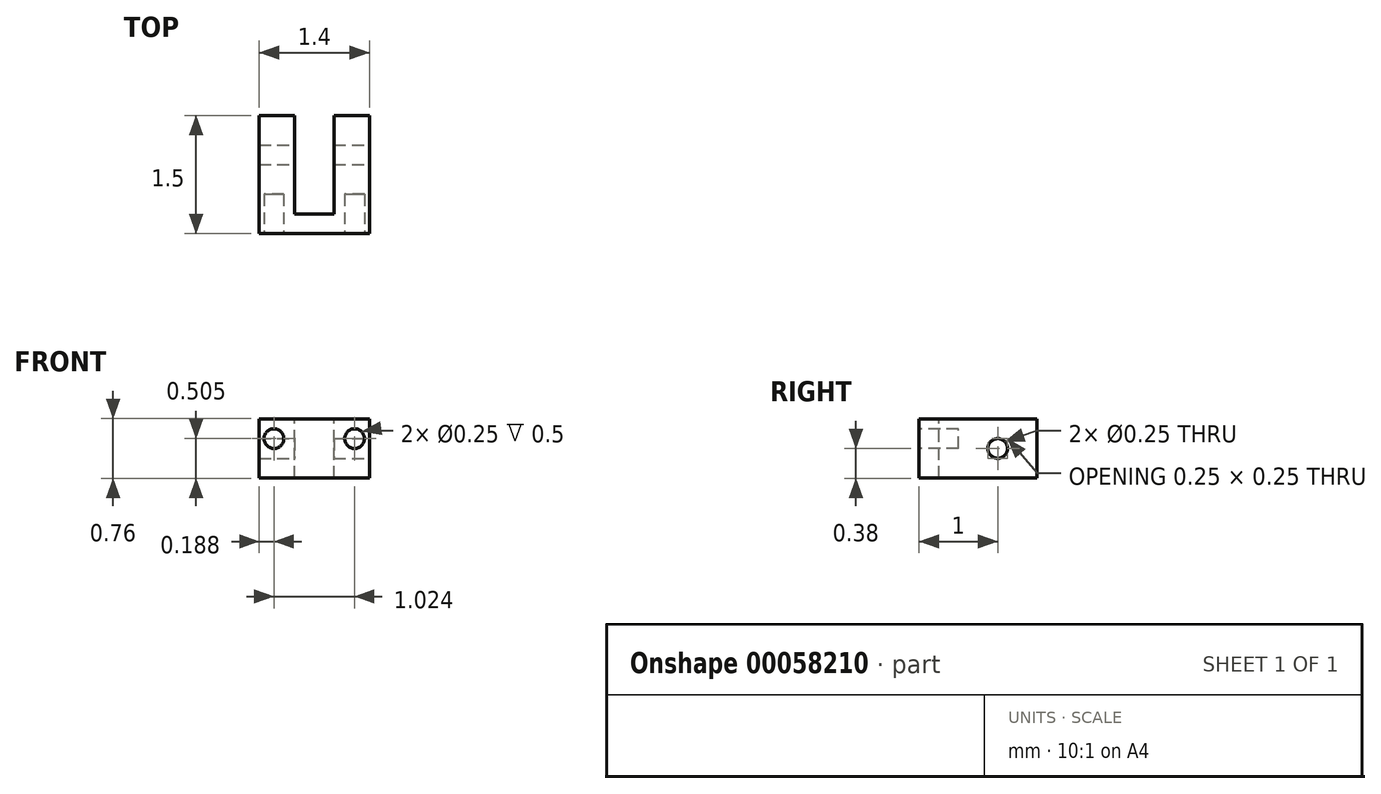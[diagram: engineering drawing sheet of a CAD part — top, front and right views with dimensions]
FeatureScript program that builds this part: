
annotation { "Feature Type Name" : "Feature", "Feature Type Description" : "" }
export const myFeature = defineFeature(function(context is Context, id is Id, definition is map)
    precondition{}
    {
        {
            var Q0;
            Q0=qCreatedBy(makeId("Front.planeOp"),FACE);
            var sketch = newSketch(context, id + "F0", { "sketchPlane" : qUnion([Q0])});
            skLineSegment(sketch, "E0.rect.bottom", {"start": v(0.7, 0.37) * mm, "end": v(-0.7, 0.37) * mm});
            skLineSegment(sketch, "E0.rect.top", {"start": v(0.7, -0.38) * mm, "end": v(-0.7, -0.38) * mm});
            skLineSegment(sketch, "E0.rect.left", {"start": v(0.7, 0.37) * mm, "end": v(0.7, -0.38) * mm});
            skLineSegment(sketch, "E0.rect.right", {"start": v(-0.7, 0.37) * mm, "end": v(-0.7, -0.38) * mm});
            skPoint(sketch, "E0.rect.middle", {"position": v(0, 0) * mm});
            skSolve(sketch);
        }
        {
            var Q0;
            Q0=qSketchRegion(id+"F0",true);
            extrude(context, id + "F1", {"entities" : qUnion([Q0]), "endBound" : BoundingType.SYMMETRIC, "depth" : 1.5 * mm});
        }
        {
            var Q0;
            Q0=makeQuery(id+"F1.opExtrude","SWEPT_FACE",FACE,{"disambiguationData":[OSD([sQuery(id+"F0.wireOp",EDGE,"E0.rect.left")])]});
            var sketch = newSketch(context, id + "F2", { "sketchPlane" : qUnion([Q0])});
            skCircle(sketch, "E1", {"center": v(0.25, 0) * mm, "radius": 0.12 * mm});
            skSolve(sketch);
        }
        {
            var Q0;
            Q0=qSketchRegion(id+"F2",true);
            extrude(context, id + "F3", {"entities" : qUnion([Q0]), "operationType" : NewBodyOperationType.REMOVE, "oppositeDirection" : true, "depth" : 25 * mm});
        }
        {
            var Q0;
            Q0=makeQuery(id+"F1.opExtrude","SWEPT_FACE",FACE,{"disambiguationData":[OSD([sQuery(id+"F0.wireOp",EDGE,"E0.rect.bottom")])]});
            var sketch = newSketch(context, id + "F4", { "sketchPlane" : qUnion([Q0])});
            skLineSegment(sketch, "E2.bottom", {"start": v(-0.25, 0.75) * mm, "end": v(0.25, 0.75) * mm});
            skLineSegment(sketch, "E2.top", {"start": v(-0.25, -0.5) * mm, "end": v(0.25, -0.5) * mm});
            skLineSegment(sketch, "E2.left", {"start": v(-0.25, 0.75) * mm, "end": v(-0.25, -0.5) * mm});
            skLineSegment(sketch, "E2.right", {"start": v(0.25, 0.75) * mm, "end": v(0.25, -0.5) * mm});
            skSolve(sketch);
        }
        {
            var Q0;
            Q0=qSketchRegion(id+"F4",true);
            extrude(context, id + "F5", {"entities" : qUnion([Q0]), "operationType" : NewBodyOperationType.REMOVE, "endBound" : BoundingType.SYMMETRIC, "oppositeDirection" : true, "depth" : 25 * mm});
        }
        {
            var Q0;
            Q0=makeQuery(id+"F1.opExtrude","CAP_FACE",FACE,{"disambiguationData":[OSD([sQuery(id+"F0.wireOp",EDGE,"E0.rect.bottom"),sQuery(id+"F0.wireOp",EDGE,"E0.rect.top"),sQuery(id+"F0.wireOp",EDGE,"E0.rect.left"),sQuery(id+"F0.wireOp",EDGE,"E0.rect.right")])],"isStart":false});
            var sketch = newSketch(context, id + "F6", { "sketchPlane" : qUnion([Q0])});
            skCircle(sketch, "E3", {"center": v(0.51, 0.12) * mm, "radius": 0.12 * mm});
            skCircle(sketch, "E4", {"center": v(-0.51, 0.12) * mm, "radius": 0.12 * mm});
            skSolve(sketch);
        }
        {
            var Q0;
            Q0=qSketchRegion(id+"F6",true);
            extrude(context, id + "F7", {"entities" : qUnion([Q0]), "operationType" : NewBodyOperationType.REMOVE, "oppositeDirection" : true, "depth" : 0.5 * mm});
        }
    });
